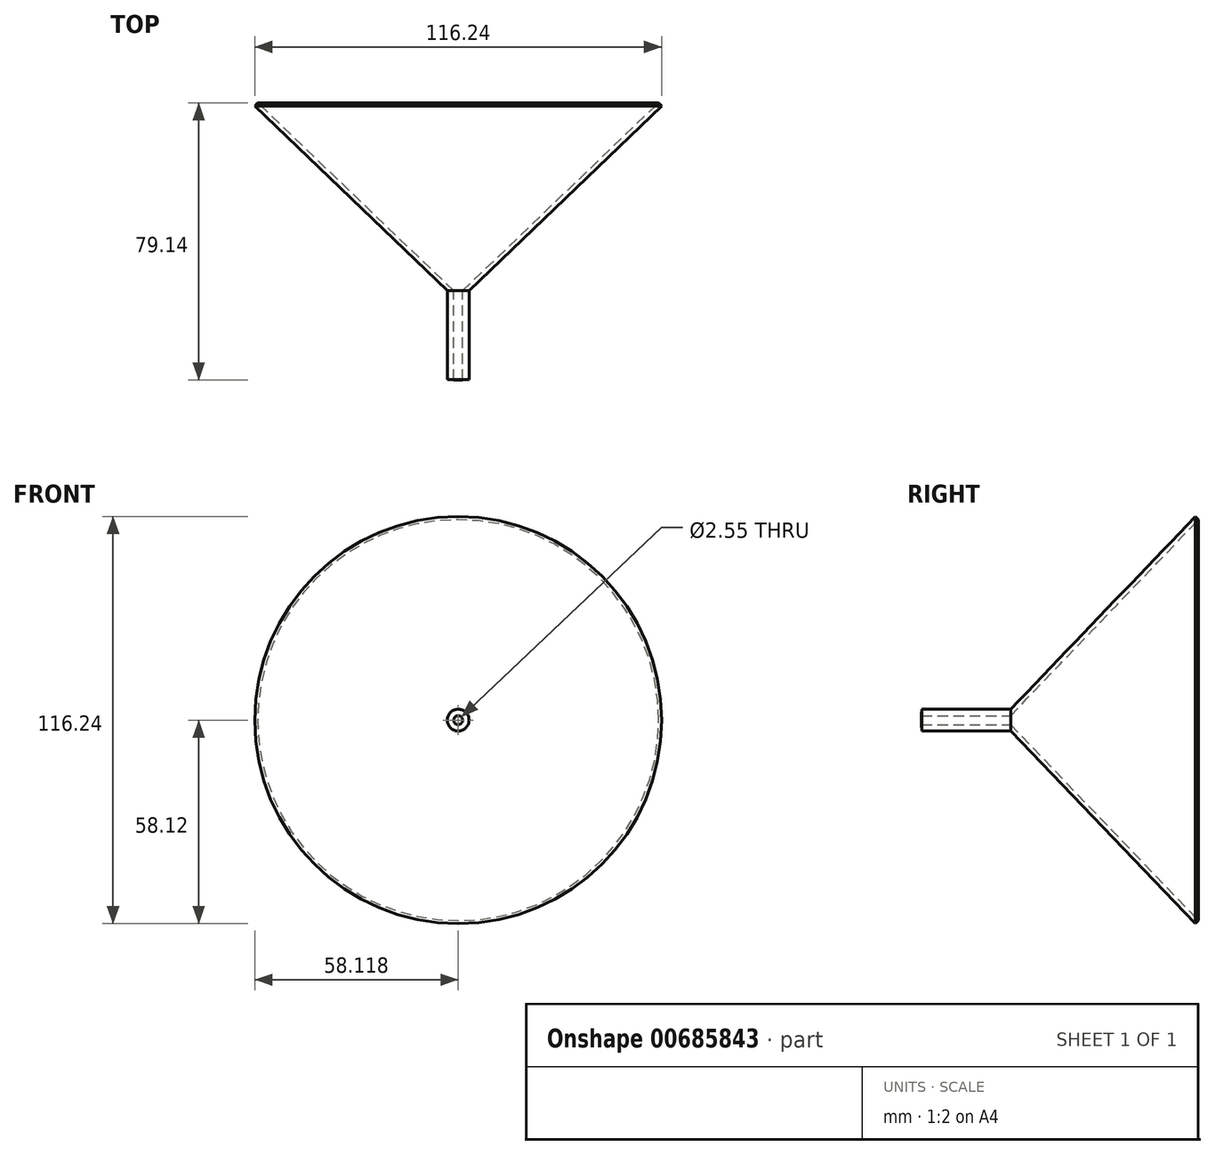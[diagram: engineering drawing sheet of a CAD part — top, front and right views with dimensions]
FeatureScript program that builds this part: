
annotation { "Feature Type Name" : "Feature", "Feature Type Description" : "" }
export const myFeature = defineFeature(function(context is Context, id is Id, definition is map)
    precondition{}
    {
        {
            var Q0;
            Q0=qCreatedBy(makeId("Top.planeOp"),FACE);
            var sketch = newSketch(context, id + "F0", { "sketchPlane" : qUnion([Q0])});
            skLineSegment(sketch, "E0", {"start": v(0, 0) * mm, "end": v(55, 52.73) * mm});
            skLineSegment(sketch, "E1", {"start": v(55, 52.73) * mm, "end": v(54.13, 53.65) * mm});
            skLineSegment(sketch, "E2", {"start": v(54.13, 53.65) * mm, "end": v(-1.84, 0) * mm});
            skLineSegment(sketch, "E3", {"start": v(-1.84, 0) * mm, "end": v(0, 0) * mm});
            skLineSegment(sketch, "E4", {"start": v(0, 0) * mm, "end": v(0, -25.4) * mm});
            skLineSegment(sketch, "E5", {"start": v(0, -25.4) * mm, "end": v(0, 0) * mm});
            skLineSegment(sketch, "E6", {"start": v(-1.84, 0) * mm, "end": v(-1.84, -25.5) * mm});
            skLineSegment(sketch, "E7", {"start": v(-1.84, -25.5) * mm, "end": v(0, -25.4) * mm});
            skLineSegment(sketch, "E8", {"start": v(-3.11, 0) * mm, "end": v(-3.11, -25.4) * mm});
            skSolve(sketch);
        }
        {
            var Q0;
            Q0=makeQuery(id+"F0.imprint","IMPRINT",FACE,{"disambiguationData":[TD([[makeQuery(id+"F0.imprint","IMPRINT",EDGE,{"derivedFrom":sQuery(id+"F0.wireOp",EDGE,"E3")}),-1.0]])]});
            var Q1;
            Q1=makeQuery(id+"F0.imprint","IMPRINT",FACE,{"disambiguationData":[TD([[makeQuery(id+"F0.imprint","IMPRINT",EDGE,{"derivedFrom":sQuery(id+"F0.wireOp",EDGE,"E0")}),1.0]])]});
            var Q2;
            Q2=sQuery(id+"F0.wireOp",EDGE,"E8");
            revolve(context, id + "F1", {"entities" : qUnion([Q0, Q1]), "axis" : qUnion([Q2]), "revolveType" : RevolveType.FULL});
        }
    });
